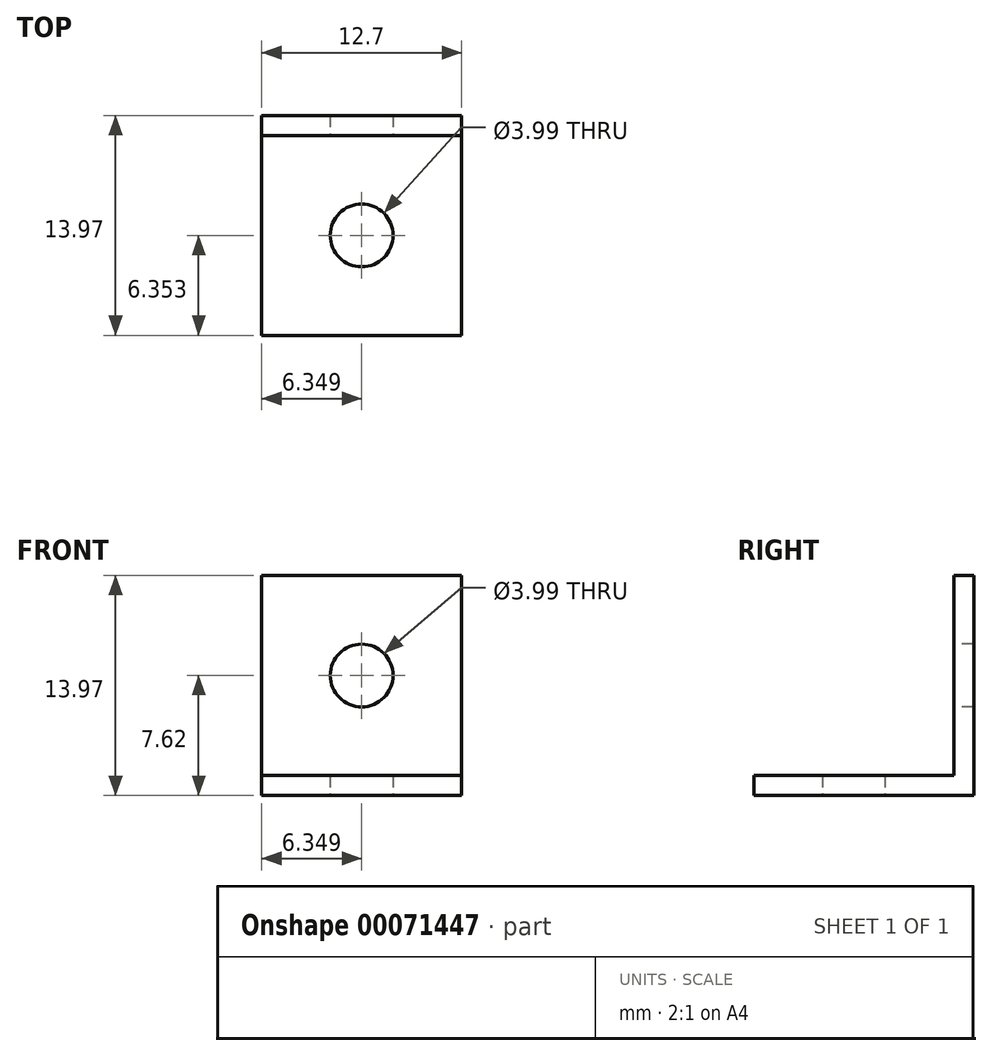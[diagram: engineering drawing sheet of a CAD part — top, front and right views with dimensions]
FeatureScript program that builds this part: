
annotation { "Feature Type Name" : "Feature", "Feature Type Description" : "" }
export const myFeature = defineFeature(function(context is Context, id is Id, definition is map)
    precondition{}
    {
        {
            var Q0;
            Q0=qCreatedBy(makeId("Top.planeOp"),FACE);
            var sketch = newSketch(context, id + "F0", { "sketchPlane" : qUnion([Q0])});
            skLineSegment(sketch, "E0.bottom", {"start": v(-47.58, 37.85) * mm, "end": v(-34.88, 37.85) * mm});
            skLineSegment(sketch, "E0.top", {"start": v(-47.58, 23.88) * mm, "end": v(-34.88, 23.88) * mm});
            skLineSegment(sketch, "E0.left", {"start": v(-47.58, 37.85) * mm, "end": v(-47.58, 23.88) * mm});
            skLineSegment(sketch, "E0.right", {"start": v(-34.88, 37.85) * mm, "end": v(-34.88, 23.88) * mm});
            skCircle(sketch, "E1", {"center": v(-41.23, 30.23) * mm, "radius": 2 * mm});
            skSolve(sketch);
        }
        {
            var Q0;
            Q0=makeQuery(id+"F0.imprint","IMPRINT",FACE,{"disambiguationData":[TD([[makeQuery(id+"F0.imprint","IMPRINT",EDGE,{"derivedFrom":sQuery(id+"F0.wireOp",EDGE,"E0.bottom")}),-1.0]])]});
            extrude(context, id + "F1", {"entities" : qUnion([Q0]), "depth" : 13.97 * mm});
        }
        {
            var Q0;
            Q0=makeQuery(id+"F1.opExtrude","CAP_FACE",FACE,{"disambiguationData":[OSD([sQuery(id+"F0.wireOp",EDGE,"E0.bottom"),sQuery(id+"F0.wireOp",EDGE,"E0.top"),sQuery(id+"F0.wireOp",EDGE,"E0.left"),sQuery(id+"F0.wireOp",EDGE,"E0.right"),sQuery(id+"F0.wireOp",EDGE,"E1")])],"isStart":false});
            var sketch = newSketch(context, id + "F2", { "sketchPlane" : qUnion([Q0])});
            skLineSegment(sketch, "E2", {"start": v(-47.58, 36.58) * mm, "end": v(-34.88, 36.58) * mm});
            skLineSegment(sketch, "E3", {"start": v(-47.58, 36.58) * mm, "end": v(-47.58, 23.88) * mm});
            skLineSegment(sketch, "E4", {"start": v(-47.58, 23.88) * mm, "end": v(-34.88, 23.88) * mm});
            skLineSegment(sketch, "E5", {"start": v(-34.88, 23.88) * mm, "end": v(-34.88, 36.58) * mm});
            skSolve(sketch);
        }
        {
            var Q0;
            Q0=makeQuery(id+"F2.imprint","IMPRINT",FACE,{"disambiguationData":[TD([[makeQuery(id+"F2.imprint","IMPRINT",EDGE,{"derivedFrom":sQuery(id+"F2.wireOp",EDGE,"E2")}),-1.0]])]});
            extrude(context, id + "F3", {"entities" : qUnion([Q0]), "operationType" : NewBodyOperationType.REMOVE, "oppositeDirection" : true, "depth" : 12.7 * mm});
        }
        {
            var Q0;
            Q0=makeQuery(id+"F3.boolean.opBoolean","COPY",FACE,{"derivedFrom":makeQuery(id+"F3.opExtrude","SWEPT_FACE",FACE,{"disambiguationData":[OSD([sQuery(id+"F2.wireOp",EDGE,"E2")])]})});
            var sketch = newSketch(context, id + "F4", { "sketchPlane" : qUnion([Q0])});
            skCircle(sketch, "E6", {"center": v(-41.23, 7.62) * mm, "radius": 2 * mm});
            skSolve(sketch);
        }
        {
            var Q0;
            Q0=makeQuery(id+"F4.imprint","IMPRINT",FACE,{"disambiguationData":[TD([[makeQuery(id+"F4.imprint","IMPRINT",EDGE,{"derivedFrom":sQuery(id+"F4.wireOp",EDGE,"E6")}),1.0]])]});
            extrude(context, id + "F5", {"entities" : qUnion([Q0]), "operationType" : NewBodyOperationType.REMOVE, "oppositeDirection" : true, "depth" : 25.4 * mm});
        }
    });
